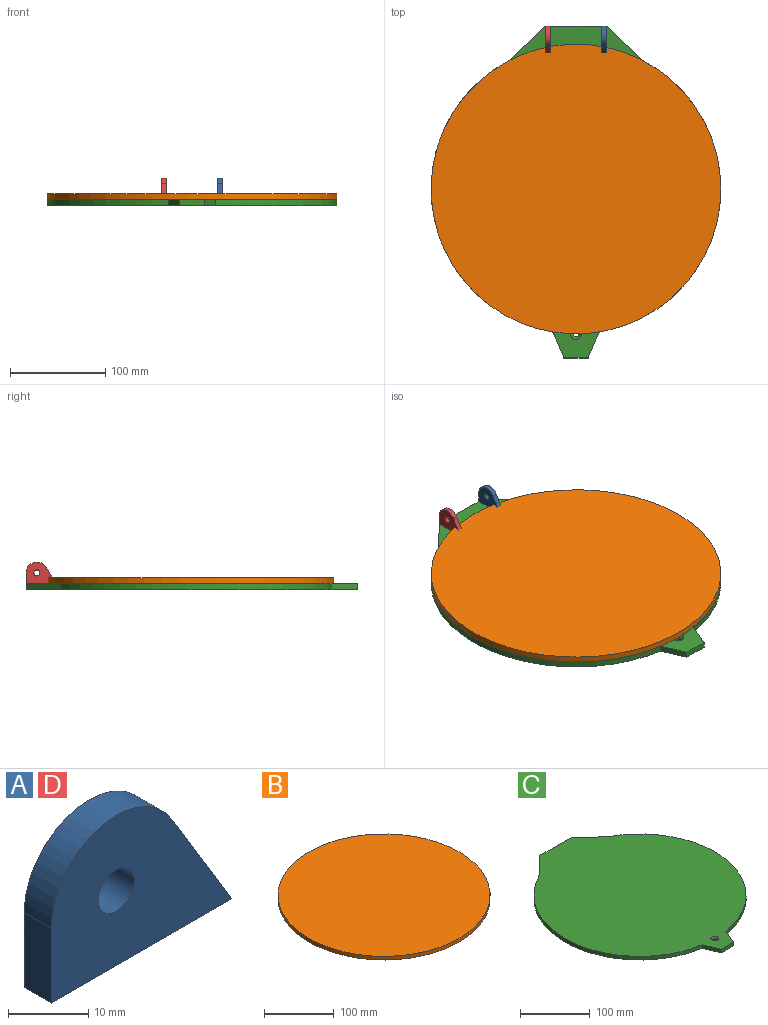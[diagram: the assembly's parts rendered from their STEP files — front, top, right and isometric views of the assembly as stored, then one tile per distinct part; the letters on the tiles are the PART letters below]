
ASSEMBLY  parts=4 mates=3
PART A: 7 faces, bbox 31.8x4.8x22.9 mm
  f0: plane 31.75x4.76mm, normal (0,0,-1), area 151.2mm2, adj f1,f3,f4,f5
  f1: plane 17.36x10.52mm, normal (0.86,0,0.52), area 96.7mm2, adj f0,f2,f4,f5
  f2: cylinder r=11.44mm len=21.23mm, axis (0,-1,0), area 141.9mm2, adj f1,f3,f4,f5
  f3: plane 11.35x4.76mm, normal (-1,0,0), area 54.1mm2, adj f0,f2,f4,f5
  f4: plane 31.75x22.87mm, normal (0,1,0), area 501.3mm2, adj f0,f1,f2,f3,f6
  f5: plane 31.75x22.87mm, normal (0,-1,0), area 501.3mm2, adj f0,f1,f2,f3,f6
  f6: cylinder r=3.17mm len=6.35mm, axis (0,-1,0), area 95mm2, adj f4,f5
PART B: 3 faces, bbox 304.8x304.8x6.4 mm
  f0: cylinder r=152.4mm len=304.8mm, axis (0,0,-1), area 6080.5mm2, adj f1,f2
  f1: plane 304.8x304.8mm, normal (0,0,1), area 72965.9mm2, adj f0
  f2: plane 304.8x304.8mm, normal (0,0,-1), area 72965.9mm2, adj f0
PART C: 12 faces, bbox 304.8x349.3x6.4 mm
  f0: cylinder r=152.4mm len=285.96mm, axis (0,0,-1), area 2425.5mm2, adj f2,f3,f6,f9
  f1: cylinder r=152.4mm len=285.96mm, axis (0,0,-1), area 2425.5mm2, adj f2,f3,f5,f7
  f2: plane 349.25x304.8mm, normal (0,0,1), area 75869.7mm2, adj f0,f1,f4,f5,f6,f7,f8,f9
  f3: plane 349.25x304.8mm, normal (0,0,-1), area 75940.6mm2, adj f0,f1,f4,f5,f6,f7,f8,f9
  f4: plane 63.5x6.35mm, normal (0,1,0), area 403.2mm2, adj f2,f3,f5,f6
  f5: plane 38.01x35.95mm, normal (-0.69,0.73,0), area 332.2mm2, adj f1,f2,f3,f4
  f6: plane 38.01x35.95mm, normal (0.69,0.73,0), area 332.2mm2, adj f0,f2,f3,f4
  f7: plane 27.34x11.55mm, normal (-0.92,-0.39,0), area 188.5mm2, adj f1,f2,f3,f8
  f8: plane 25.4x6.35mm, normal (0,-1,0), area 161.3mm2, adj f2,f3,f7,f9
  f9: plane 27.34x11.55mm, normal (0.92,-0.39,0), area 188.5mm2, adj f0,f2,f3,f8
  f10: cylinder r=3.17mm len=6.35mm, axis (0,0,1), area 76mm2, adj f3,f11
  f11: cone r=3.17mm half-angle=45deg, axis (0,0,1), area 100.3mm2, adj f2,f10
PART D: same geometry as A
PLACE A rot(axis=(0,0,-1),90deg) t=(12.46,142.02,-15.16)mm
PLACE B t=(-14.53,-17.52,-15.16)mm
PLACE C t=(-14.53,-17.44,-21.51)mm fixed
PLACE D rot(axis=(0,0,-1),90deg) t=(-46.28,142.02,-15.16)mm
MATE fastened D.f0 <-> C.f2  axis (0,0,1) through (-46.28,154.01,-15.16)mm
MATE fastened C.f2 <-> A.f0  axis (0,0,1) through (17.22,154.01,-15.16)mm
MATE fastened B.f0 <-> C.f2  axis (0,0,-1) through (-14.53,-17.52,-15.16)mm
